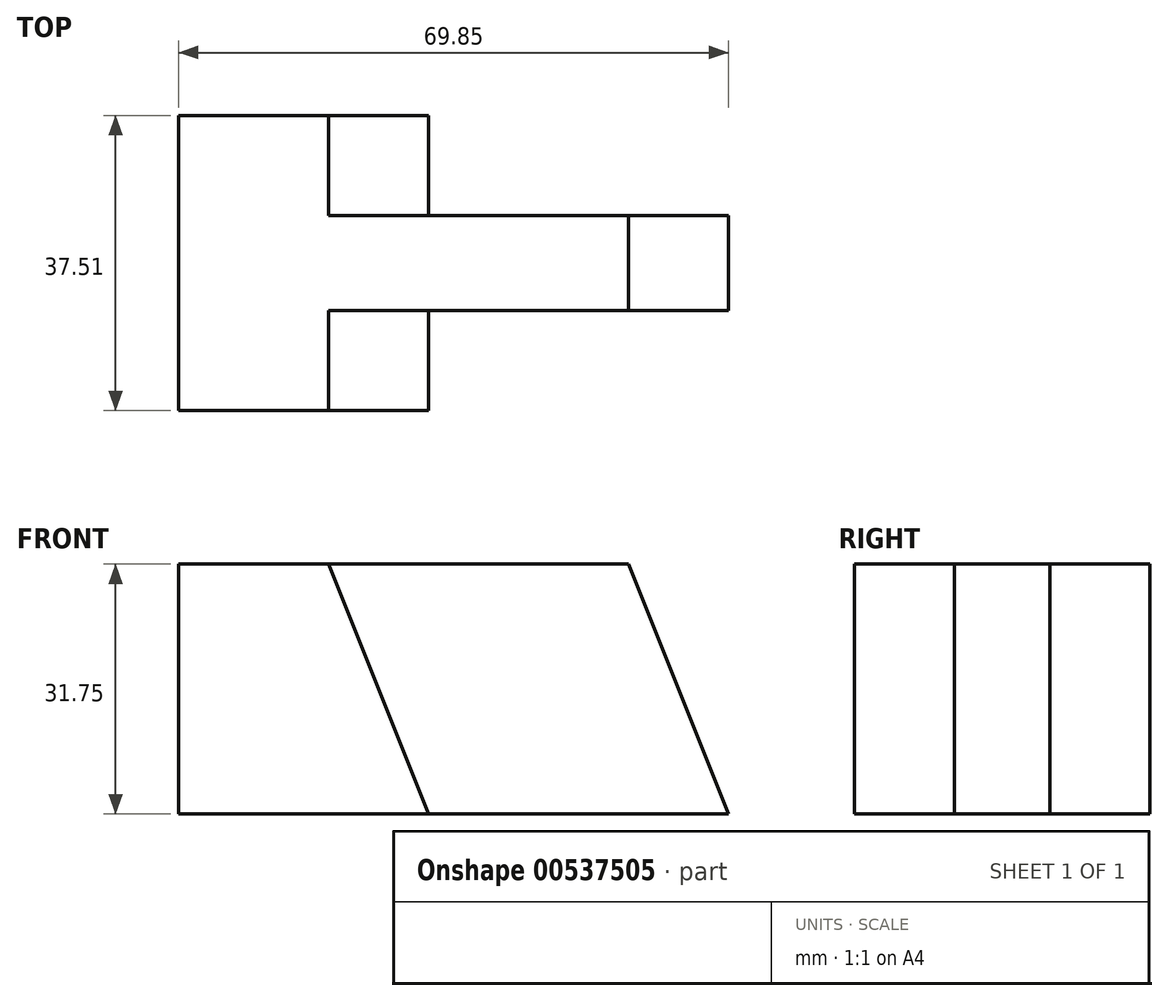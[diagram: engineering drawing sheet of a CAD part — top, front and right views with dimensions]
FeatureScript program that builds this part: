
annotation { "Feature Type Name" : "Feature", "Feature Type Description" : "" }
export const myFeature = defineFeature(function(context is Context, id is Id, definition is map)
    precondition{}
    {
        {
            var Q0;
            Q0=qCreatedBy(makeId("Top.planeOp"),FACE);
            var sketch = newSketch(context, id + "F0", { "sketchPlane" : qUnion([Q0])});
            skLineSegment(sketch, "E0", {"start": v(0, 0) * mm, "end": v(0, 37.52) * mm});
            skLineSegment(sketch, "E1", {"start": v(-0.62, 37.5) * mm, "end": v(31.75, 37.5) * mm});
            skLineSegment(sketch, "E2", {"start": v(31.75, 37.5) * mm, "end": v(31.75, 24.8) * mm});
            skLineSegment(sketch, "E3", {"start": v(31.75, 24.8) * mm, "end": v(69.85, 24.8) * mm});
            skLineSegment(sketch, "E4", {"start": v(69.85, 24.8) * mm, "end": v(69.85, 12.7) * mm});
            skLineSegment(sketch, "E5", {"start": v(69.85, 12.7) * mm, "end": v(31.75, 12.7) * mm});
            skLineSegment(sketch, "E6", {"start": v(31.75, 12.7) * mm, "end": v(31.75, 0) * mm});
            skLineSegment(sketch, "E7", {"start": v(31.75, 0) * mm, "end": v(0, 0) * mm});
            skSolve(sketch);
        }
        {
            var Q0;
            {var subQ0=sQuery(id+"F0.wireOp",EDGE,"E2");Q0=makeQuery(id+"F0.imprint","IMPRINT",FACE,{"disambiguationData":[TD([[makeQuery(id+"F0.imprint","IMPRINT",EDGE,{"derivedFrom":subQ0}),-1.0]])]});}
            extrude(context, id + "F1", {"entities" : qUnion([Q0]), "depth" : 31.75 * mm, "offsetDistance" : 25.4 * mm});
        }
        {
            var Q0;
            Q0=makeQuery(id+"F1.opExtrude","SWEPT_FACE",FACE,{"disambiguationData":[OSD([sQuery(id+"F0.wireOp",EDGE,"E5")])]});
            var sketch = newSketch(context, id + "F2", { "sketchPlane" : qUnion([Q0])});
            skLineSegment(sketch, "E8", {"start": v(69.85, 0) * mm, "end": v(57.15, 31.75) * mm});
            skSolve(sketch);
        }
        {
            var Q0;
            {var subQ0=sQuery(id+"F2.wireOp",EDGE,"E8");Q0=makeQuery(id+"F2.imprint","IMPRINT",FACE,{"disambiguationData":[TD([[makeQuery(id+"F2.imprint","IMPRINT",EDGE,{"derivedFrom":subQ0}),-1.0]])]});}
            extrude(context, id + "F3", {"entities" : qUnion([Q0]), "operationType" : NewBodyOperationType.REMOVE, "oppositeDirection" : true, "depth" : 25.4 * mm, "offsetDistance" : 25.4 * mm});
        }
        {
            var Q0;
            Q0=makeQuery(id+"F1.opExtrude","SWEPT_FACE",FACE,{"disambiguationData":[OSD([sQuery(id+"F0.wireOp",EDGE,"E7")])]});
            var sketch = newSketch(context, id + "F4", { "sketchPlane" : qUnion([Q0])});
            skLineSegment(sketch, "E9", {"start": v(31.75, 0) * mm, "end": v(19.05, 31.75) * mm});
            skSolve(sketch);
        }
        {
            var Q0;
            {var subQ0=sQuery(id+"F4.wireOp",EDGE,"E9");Q0=makeQuery(id+"F4.imprint","IMPRINT",FACE,{"disambiguationData":[TD([[makeQuery(id+"F4.imprint","IMPRINT",EDGE,{"derivedFrom":subQ0}),-1.0]])]});}
            extrude(context, id + "F5", {"entities" : qUnion([Q0]), "operationType" : NewBodyOperationType.REMOVE, "oppositeDirection" : true, "depth" : 12.7 * mm, "offsetDistance" : 25.4 * mm});
        }
        {
            var Q0;
            Q0=makeQuery(id+"F1.opExtrude","SWEPT_FACE",FACE,{"disambiguationData":[OSD([sQuery(id+"F0.wireOp",EDGE,"E1")])]});
            var sketch = newSketch(context, id + "F6", { "sketchPlane" : qUnion([Q0])});
            skLineSegment(sketch, "E10", {"start": v(-31.75, 0) * mm, "end": v(-19.05, 31.75) * mm});
            skSolve(sketch);
        }
        {
            var Q0;
            {var subQ0=sQuery(id+"F6.wireOp",EDGE,"E10");Q0=makeQuery(id+"F6.imprint","IMPRINT",FACE,{"disambiguationData":[TD([[makeQuery(id+"F6.imprint","IMPRINT",EDGE,{"derivedFrom":subQ0}),1.0]])]});}
            extrude(context, id + "F7", {"entities" : qUnion([Q0]), "operationType" : NewBodyOperationType.ADD, "depth" : 12.7 * mm, "offsetDistance" : 25.4 * mm});
        }
        {
            var Q0;
            Q0=makeQuery(id+"F7.opExtrude","CAP_FACE",FACE,{"disambiguationData":[OSD([sQuery(id+"F0.wireOp",EDGE,"E1"),sQuery(id+"F0.wireOp",EDGE,"E2"),sQuery(id+"F6.wireOp",EDGE,"E10")])],"isStart":false});
            extrude(context, id + "F8", {"entities" : qUnion([Q0]), "operationType" : NewBodyOperationType.REMOVE, "oppositeDirection" : true, "depth" : 25.4 * mm, "offsetDistance" : 25.4 * mm});
        }
    });
